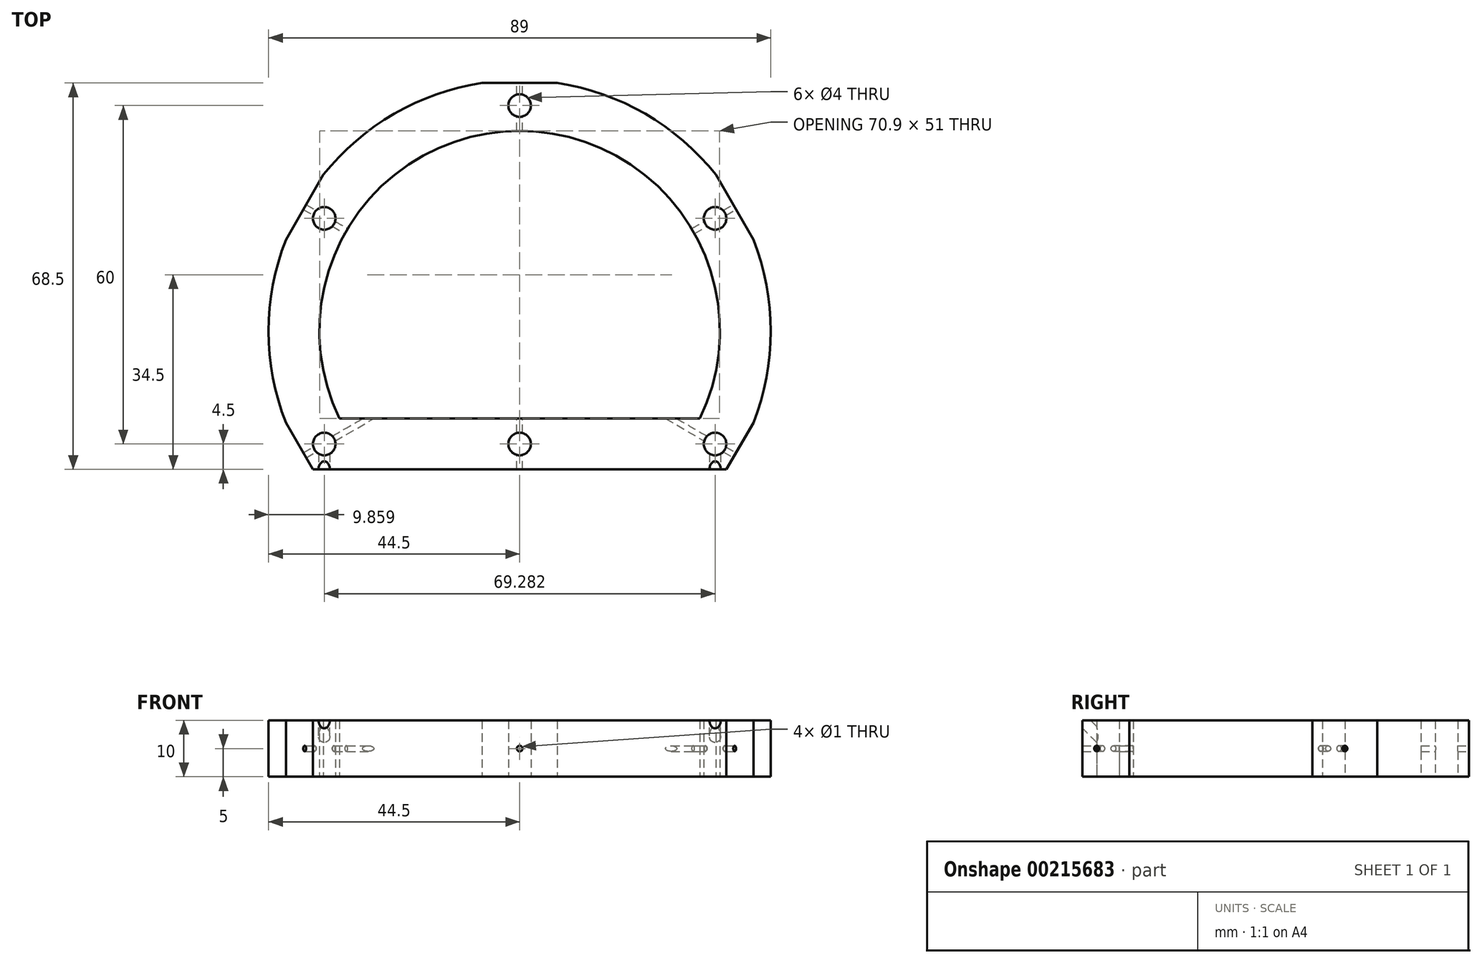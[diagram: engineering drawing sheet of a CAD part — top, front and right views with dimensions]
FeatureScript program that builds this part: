
annotation { "Feature Type Name" : "Feature", "Feature Type Description" : "" }
export const myFeature = defineFeature(function(context is Context, id is Id, definition is map)
    precondition{}
    {
        {
            var Q0;
            Q0=qCreatedBy(makeId("Top.planeOp"),FACE);
            var sketch = newSketch(context, id + "F0", { "sketchPlane" : qUnion([Q0])});
            skCircle(sketch, "E0", {"center": v(0, 0) * mm, "radius": 40 * mm, "construction": true});
            skLineSegment(sketch, "E1", {"start": v(0, 40) * mm, "end": v(-34.64, -20) * mm, "construction": true});
            skLineSegment(sketch, "E2", {"start": v(-34.64, -20) * mm, "end": v(34.64, -20) * mm, "construction": true});
            skLineSegment(sketch, "E3", {"start": v(34.64, -20) * mm, "end": v(0, 40) * mm, "construction": true});
            skLineSegment(sketch, "E4", {"start": v(-34.64, 20) * mm, "end": v(34.64, 20) * mm, "construction": true});
            skLineSegment(sketch, "E5", {"start": v(34.64, 20) * mm, "end": v(0, -40) * mm, "construction": true});
            skLineSegment(sketch, "E6", {"start": v(0, -40) * mm, "end": v(-34.64, 20) * mm, "construction": true});
            skArc(sketch, "E7", {"start": v(41.43, -16.24) * mm, "mid": v(44.5, 0) * mm, "end": v(41.43, 16.24) * mm});
            skCircle(sketch, "E8", {"center": v(0, 40) * mm, "radius": 2 * mm});
            skCircle(sketch, "E9", {"center": v(-34.64, -20) * mm, "radius": 2 * mm});
            skCircle(sketch, "E10", {"center": v(34.64, -20) * mm, "radius": 2 * mm});
            skLineSegment(sketch, "E11", {"start": v(-36.66, -24.5) * mm, "end": v(36.66, -24.5) * mm});
            skLineSegment(sketch, "E12", {"start": v(-31.94, -15.5) * mm, "end": v(31.94, -15.5) * mm});
            skArc(sketch, "E13.trimOffspring", {"start": v(31.94, -15.5) * mm, "mid": v(0, 35.5) * mm, "end": v(-31.94, -15.5) * mm});
            skCircle(sketch, "E14", {"center": v(-34.64, 20) * mm, "radius": 2 * mm});
            skCircle(sketch, "E15", {"center": v(34.64, 20) * mm, "radius": 2 * mm});
            skCircle(sketch, "E16", {"center": v(0, -20) * mm, "radius": 2 * mm});
            skLineSegment(sketch, "E17", {"start": v(-6.65, 44) * mm, "end": v(6.65, 44) * mm});
            skArc(sketch, "E18.trimOffspring", {"start": v(-6.65, 44) * mm, "mid": v(-22.25, 38.54) * mm, "end": v(-34.78, 27.76) * mm});
            skLineSegment(sketch, "E19", {"start": v(-41.43, 16.24) * mm, "end": v(-34.78, 27.76) * mm});
            skLineSegment(sketch, "E20", {"start": v(-34.64, 20) * mm, "end": v(0, 0) * mm, "construction": true});
            skLineSegment(sketch, "E21", {"start": v(0, 0) * mm, "end": v(34.64, 20) * mm, "construction": true});
            skLineSegment(sketch, "E22", {"start": v(0, 0) * mm, "end": v(34.64, -20) * mm, "construction": true});
            skLineSegment(sketch, "E23", {"start": v(0, 0) * mm, "end": v(-34.64, -20) * mm, "construction": true});
            skLineSegment(sketch, "E24", {"start": v(-41.43, -16.24) * mm, "end": v(-36.66, -24.5) * mm});
            skLineSegment(sketch, "E25", {"start": v(34.78, 27.76) * mm, "end": v(41.43, 16.24) * mm});
            skLineSegment(sketch, "E26", {"start": v(41.43, -16.24) * mm, "end": v(36.66, -24.5) * mm});
            skArc(sketch, "E27.trimOffspring", {"start": v(34.78, 27.76) * mm, "mid": v(22.25, 38.54) * mm, "end": v(6.65, 44) * mm});
            skArc(sketch, "E28.trimOffspring", {"start": v(-41.43, 16.24) * mm, "mid": v(-44.5, 0) * mm, "end": v(-41.43, -16.24) * mm});
            skSolve(sketch);
        }
        {
            var Q0;
            Q0 = qSketchRegion(id + "F0", true);
            extrude(context, id + "F1", {"entities" : qUnion([Q0]), "depth" : 10 * mm});
        }
        {
            var Q0;
            Q0=makeQuery(id+"F1.opExtrude","CAP_EDGE",EDGE,{"disambiguationData":[OSD([sQuery(id+"F0.wireOp",EDGE,"E11")])],"isStart":false});
            cPlane(context, id + "F2", {"entities" : qUnion([Q0]), "cplaneType" : CPlaneType.LINE_ANGLE, "offset" : 25 * mm, "angle" : 135 * degree, "width" : 150 * mm, "height" : 150 * mm});
        }
        {
            var Q0;
            Q0=qCreatedBy(id+"F2.planeOp",FACE);
            var sketch = newSketch(context, id + "F3", { "sketchPlane" : qUnion([Q0])});
            skCircle(sketch, "E29", {"center": v(-34.64, -10.25) * mm, "radius": 1 * mm});
            skCircle(sketch, "E30.MirrorC", {"center": v(34.64, -10.25) * mm, "radius": 1 * mm});
            skPoint(sketch, "E31", {"position": v(-34.64, -7.07) * mm});
            skLineSegment(sketch, "E32", {"start": v(-34.64, -7.07) * mm, "end": v(-34.64, -14.29) * mm, "construction": true});
            skSolve(sketch);
        }
        {
            var Q0;
            Q0 = qSketchRegion(id + "F3", true);
            extrude(context, id + "F4", {"entities" : qUnion([Q0]), "operationType" : NewBodyOperationType.REMOVE, "oppositeDirection" : true, "depth" : 5 * mm});
        }
        {
            var Q0;
            Q0=makeQuery(id+"F1.opExtrude","SWEPT_FACE",FACE,{"disambiguationData":[OSD([sQuery(id+"F0.wireOp",EDGE,"E26")])]});
            var sketch = newSketch(context, id + "F5", { "sketchPlane" : qUnion([Q0])});
            skCircle(sketch, "E33", {"center": v(0, 5) * mm, "radius": 0.5 * mm});
            skPoint(sketch, "E33.centerSnap0", {"position": v(6.65, 5) * mm});
            skSolve(sketch);
        }
        {
            var Q0;
            Q0 = qSketchRegion(id + "F5", true);
            extrude(context, id + "F6", {"entities" : qUnion([Q0]), "operationType" : NewBodyOperationType.REMOVE, "endBound" : BoundingType.THROUGH_ALL, "oppositeDirection" : true, "depth" : 15 * mm});
        }
        {
            var Q0;
            Q0=makeQuery(id+"F1.opExtrude","SWEPT_FACE",FACE,{"disambiguationData":[OSD([sQuery(id+"F0.wireOp",EDGE,"E25")])]});
            var sketch = newSketch(context, id + "F7", { "sketchPlane" : qUnion([Q0])});
            skCircle(sketch, "E34", {"center": v(0, 5) * mm, "radius": 0.5 * mm});
            skPoint(sketch, "E34.centerSnap0", {"position": v(-6.65, 5) * mm});
            skSolve(sketch);
        }
        {
            var Q0;
            Q0 = qSketchRegion(id + "F7", true);
            extrude(context, id + "F8", {"entities" : qUnion([Q0]), "operationType" : NewBodyOperationType.REMOVE, "endBound" : BoundingType.THROUGH_ALL, "oppositeDirection" : true, "depth" : 15 * mm});
        }
        {
            var Q0;
            Q0=makeQuery(id+"F1.opExtrude","SWEPT_FACE",FACE,{"disambiguationData":[OSD([sQuery(id+"F0.wireOp",EDGE,"E17")])]});
            var sketch = newSketch(context, id + "F9", { "sketchPlane" : qUnion([Q0])});
            skCircle(sketch, "E35", {"center": v(0, 5) * mm, "radius": 0.5 * mm});
            skPoint(sketch, "E35.centerSnap0", {"position": v(6.65, 5) * mm});
            skSolve(sketch);
        }
        {
            var Q0;
            Q0 = qSketchRegion(id + "F9", true);
            extrude(context, id + "F10", {"entities" : qUnion([Q0]), "operationType" : NewBodyOperationType.REMOVE, "endBound" : BoundingType.THROUGH_ALL, "oppositeDirection" : true, "depth" : 15 * mm});
        }
    });
